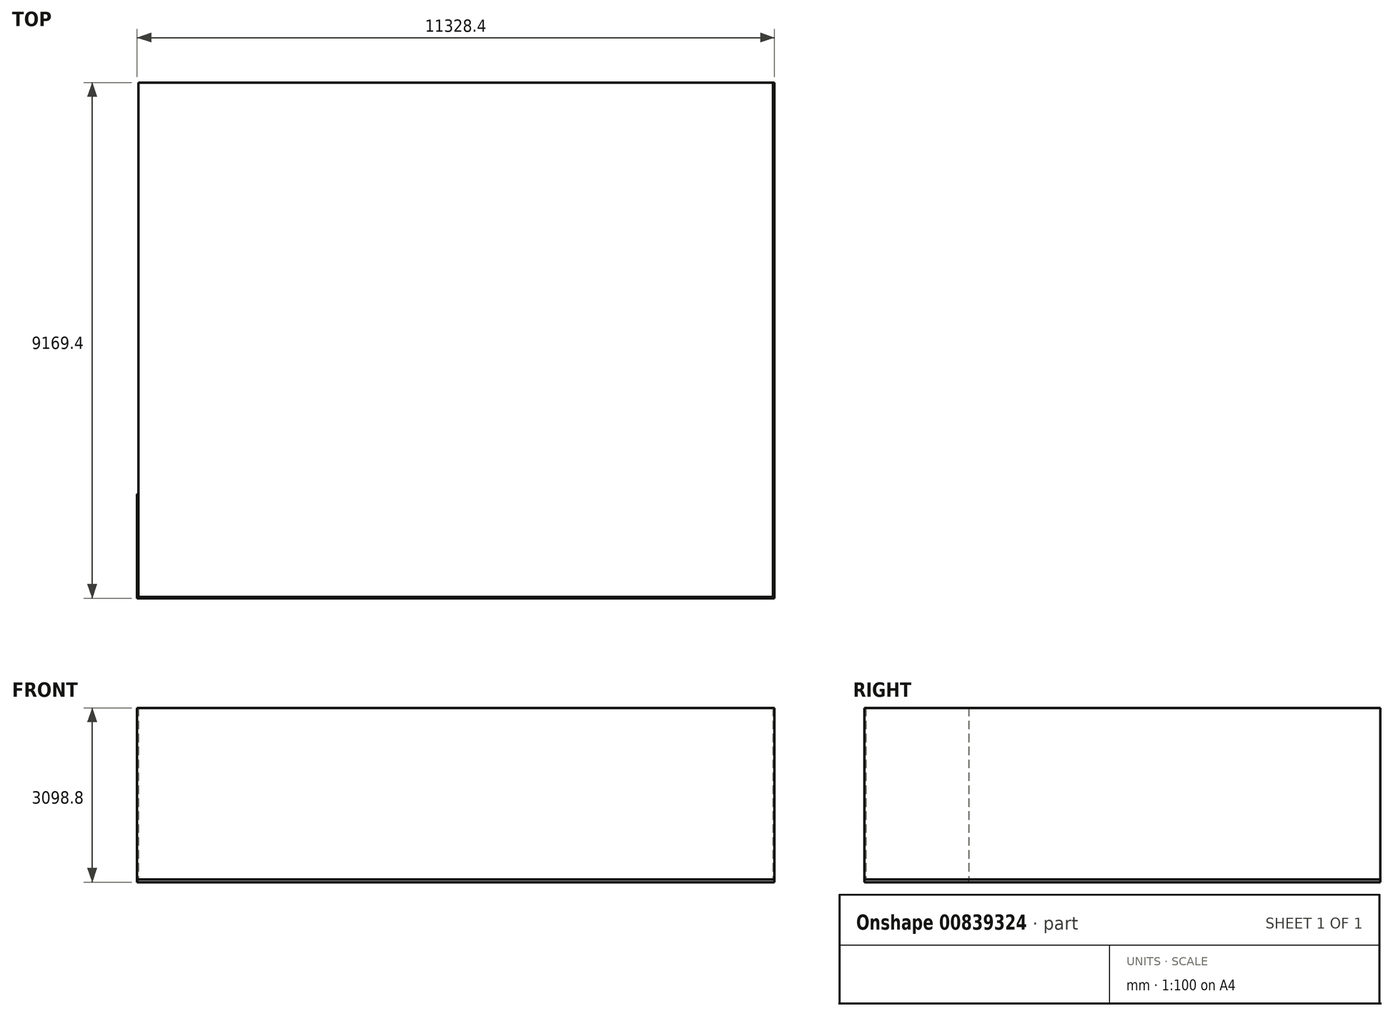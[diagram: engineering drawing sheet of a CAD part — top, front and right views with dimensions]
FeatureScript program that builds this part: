
annotation { "Feature Type Name" : "Feature", "Feature Type Description" : "" }
export const myFeature = defineFeature(function(context is Context, id is Id, definition is map)
    precondition{}
    {
        {
            assignVariable(context, id + "F0", {"name" : "height", "anyValue" : 3048 * mm});
        }
        {
            assignVariable(context, id + "F1", {"name" : "floor_thickness", "anyValue" : 50.8 * mm});
        }
        {
            var Q0;
            Q0=qCreatedBy(makeId("Top.planeOp"),FACE);
            var sketch = newSketch(context, id + "F2", { "sketchPlane" : qUnion([Q0])});
            skLineSegment(sketch, "E0.bottom", {"start": v(5638.8, -4572) * mm, "end": v(-5638.8, -4572) * mm});
            skLineSegment(sketch, "E0.top", {"start": v(5638.8, 4572) * mm, "end": v(-5638.8, 4572) * mm});
            skLineSegment(sketch, "E0.left", {"start": v(5638.8, -4572) * mm, "end": v(5638.8, 4572) * mm});
            skLineSegment(sketch, "E0.right", {"start": v(-5638.8, -4572) * mm, "end": v(-5638.8, 4572) * mm});
            skPoint(sketch, "E0.middle", {"position": v(0, 0) * mm});
            skLineSegment(sketch, "E1.bottom", {"start": v(-5638.8, -4572) * mm, "end": v(-5664.2, -4572) * mm});
            skLineSegment(sketch, "E1.top", {"start": v(-5638.8, -2743.2) * mm, "end": v(-5664.2, -2743.2) * mm});
            skLineSegment(sketch, "E1.left", {"start": v(-5638.8, -4572) * mm, "end": v(-5638.8, -2743.2) * mm});
            skLineSegment(sketch, "E1.right", {"start": v(-5664.2, -4572) * mm, "end": v(-5664.2, -2743.2) * mm});
            skLineSegment(sketch, "E2.bottom", {"start": v(5638.8, -4572) * mm, "end": v(-5664.2, -4572) * mm});
            skLineSegment(sketch, "E2.top", {"start": v(5638.8, -4597.4) * mm, "end": v(-5664.2, -4597.4) * mm});
            skLineSegment(sketch, "E2.left", {"start": v(5638.8, -4572) * mm, "end": v(5638.8, -4597.4) * mm});
            skLineSegment(sketch, "E2.right", {"start": v(-5664.2, -4572) * mm, "end": v(-5664.2, -4597.4) * mm});
            skLineSegment(sketch, "E3.bottom", {"start": v(5638.8, 4572) * mm, "end": v(5664.2, 4572) * mm});
            skLineSegment(sketch, "E3.top", {"start": v(5638.8, -4597.4) * mm, "end": v(5664.2, -4597.4) * mm});
            skLineSegment(sketch, "E3.left", {"start": v(5638.8, 4572) * mm, "end": v(5638.8, -4597.4) * mm});
            skLineSegment(sketch, "E3.right", {"start": v(5664.2, 4572) * mm, "end": v(5664.2, -4597.4) * mm});
            skSolve(sketch);
        }
        {
            var Q0;
            {var subQ3=sQuery(id+"F2.wireOp",EDGE,"E3.bottom");Q0=makeQuery(id+"F2.imprint","IMPRINT",FACE,{"disambiguationData":[TD([[makeQuery(id+"F2.imprint","IMPRINT",EDGE,{"derivedFrom":subQ3}),-1.0]])]});}
            var Q1;
            {var subQ1=sQuery(id+"F2.wireOp",EDGE,"E2.top");Q1=makeQuery(id+"F2.imprint","IMPRINT",FACE,{"disambiguationData":[TD([[makeQuery(id+"F2.imprint","IMPRINT",EDGE,{"derivedFrom":subQ1}),-1.0]])]});}
            var Q2;
            {var subQ4=sQuery(id+"F2.wireOp",EDGE,"E0.top");Q2=makeQuery(id+"F2.imprint","IMPRINT",FACE,{"disambiguationData":[TD([[makeQuery(id+"F2.imprint","IMPRINT",EDGE,{"derivedFrom":subQ4}),1.0]])]});}
            var Q3;
            Q3=makeQuery(id+"F2.imprint","IMPRINT",FACE,{"disambiguationData":[TD([[makeQuery(id+"F2.imprint","IMPRINT",EDGE,{"derivedFrom":sQuery(id+"F2.wireOp",EDGE,"E1.top")}),1.0]])]});
            extrude(context, id + "F3", {"entities" : qUnion([Q0, Q1, Q2, Q3]), "oppositeDirection" : true, "depth" : getVariable(context, 'floor_thickness'), "offsetDistance" : 25 * mm});
        }
        {
            var Q0;
            Q0=makeQuery(id+"F2.imprint","IMPRINT",FACE,{"disambiguationData":[TD([[makeQuery(id+"F2.imprint","IMPRINT",EDGE,{"derivedFrom":sQuery(id+"F2.wireOp",EDGE,"E2.top")}),-1.0]])]});
            var Q1;
            Q1=makeQuery(id+"F2.imprint","IMPRINT",FACE,{"disambiguationData":[TD([[makeQuery(id+"F2.imprint","IMPRINT",EDGE,{"derivedFrom":sQuery(id+"F2.wireOp",EDGE,"E1.top")}),1.0]])]});
            var Q2;
            {var subQ3=sQuery(id+"F2.wireOp",EDGE,"E3.bottom");Q2=makeQuery(id+"F2.imprint","IMPRINT",FACE,{"disambiguationData":[TD([[makeQuery(id+"F2.imprint","IMPRINT",EDGE,{"derivedFrom":subQ3}),-1.0]])]});}
            extrude(context, id + "F4", {"entities" : qUnion([Q0, Q1, Q2]), "depth" : getVariable(context, 'height'), "offsetDistance" : 25 * mm});
        }
    });
